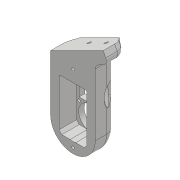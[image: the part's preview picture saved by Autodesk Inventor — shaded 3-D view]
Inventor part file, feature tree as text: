
AUTODESK INVENTOR PART (.ipt)
format: ipt  version: 2018 (Build 220112000, 112)  size: 900,608 bytes
history: native  units: mm
features: sketch x31, projected_geometry x26, extrude x24, hole x10, fillet x10, chamfer x3, mirror x1, plane x1
ambient origin geometry x8: Origin, YZ Plane, XZ Plane, XY Plane, X Axis, Y Axis, Z Axis, Center Point
bodies: Solid1 (feature_tree)
feature tree (106):
  extrude  "Extrusion1"  Depth=45.0mm
  extrude  "Extrusion2"  Depth=2.25mm
  hole  "Hole1"  [1 undecoded]
  hole  "Hole2"  [1 undecoded]
  fillet  "Fillet1"  Radius=14.0mm
  extrude  "Extrusion3"  Depth=18.5mm
  extrude  "Extrusion4"  Depth=10.0mm
  extrude  "Extrusion5"  Depth=2.195mm
  extrude  "Extrusion6"  Depth=20.5mm
  hole  "Hole3"  [1 undecoded]
  extrude  "Extrusion7"  Depth=0.5mm
  extrude  "Extrusion8"  Depth=5.0mm TaperAngle=0.0deg
  extrude  "Extrusion9"  Depth=10.0mm
  extrude  "Extrusion10"  Depth=10.0mm
  extrude  "Extrusion11"  Depth=14.5mm
  extrude  "Extrusion12"  Depth=20.0mm
  extrude  "Extrusion13"  Depth=5.0mm
  extrude  "Extrusion14"  Depth=5.0mm
  extrude  "Extrusion15"  Depth=5.0mm
  extrude  "Extrusion16"  Depth=5.0mm
  extrude  "Extrusion17"  Depth=4.0mm
  chamfer  "Chamfer1"  Distance=1.0mm
  fillet  "Fillet7"  Radius=20.7mm
  fillet  "Fillet8"  Radius=32.0mm
  mirror  "Mirror1"
  extrude  "Extrusion24"  Depth=5.0mm TaperAngle=0.0deg
  extrude  "Extrusion25"  Depth=8.0mm
  extrude  "Extrusion26"  Depth=0.2mm TaperAngle=0.0deg
  extrude  "Extrusion27"  Depth=0.5mm TaperAngle=0.0deg
  extrude  "Extrusion28"  Depth=5.0mm TaperAngle=0.0deg
  chamfer  "Chamfer5"  Distance=5.0mm
  fillet  "Fillet18"  Radius=0.2mm
  fillet  "Fillet19"  Radius=0.2mm
  extrude  "Extrusion29"  Depth=1.5mm
  chamfer  "Chamfer6"  Distance=70.0mm
  hole  "Hole10"  [1 undecoded]
  plane  "Work Plane2"
  hole  "Hole11"  [1 undecoded]
  fillet  "Fillet20"  Radius=10.0mm
  sketch  "Sketch43"  dims[d102=2.5mm d103=2.0mm d104=45.0deg d105=1.5mm]
  hole  "Hole12"  [1 undecoded]
  hole  "Hole13"  [1 undecoded]
  hole  "Hole14"  [1 undecoded]
  fillet  "Fillet21"  Radius=10.0mm
  fillet  "Fillet22"  Radius=2.0mm
  hole  "Hole15"  [1 undecoded]
  fillet  "Fillet23"  Radius=5.0mm
  hole  "Hole16"  [1 undecoded]
  fillet  "Fillet24"  Radius=15.0mm
  extrude  "Extrusion30"  Depth=10.0mm TaperAngle=0.0deg
  sketch  "Sketch1"  dims[d0=24.5mm d1=45.0mm]
  sketch  "Sketch2"  dims[d2=1.95mm d3=0.0mm d4=2.25mm]
  projected_geometry  "Projected Loop1"
  sketch  "Sketch3"  dims[d5=20.0mm d6=2.25mm]
  projected_geometry  "Projected Loop2"
  sketch  "Sketch4"  dims[d7=5.25mm d8=5.25mm d9=14.0mm]
  projected_geometry  "Projected Loop3"
  sketch  "Sketch5"  dims[d10=5.25mm d11=18.5mm]
  projected_geometry  "Projected Loop4"
  sketch  "Sketch6"  dims[d12=10.0mm d13=0.0mm d14=20.5mm]
  projected_geometry  "Projected Loop5"
  sketch  "Sketch7"  dims[d15=2.0mm d16=2.195mm]
  projected_geometry  "Projected Loop6"
  sketch  "Sketch8"  dims[d17=2.0mm]
  projected_geometry  "Projected Loop7"
  sketch  "Sketch9"  dims[d18=2.4mm d19=6.0mm d20=4.4mm d21=2.0mm d22=90.0deg d23=8.0mm d24=20.594885mm d25=20.5mm]
  projected_geometry  "Projected Loop8"
  projected_geometry  "Projected Loop9"
  sketch  "Sketch10"  dims[d26=26.65mm d27=2.0mm]
  projected_geometry  "Projected Loop10"
  projected_geometry  "Projected Loop11"
  sketch  "Sketch11"  dims[d28=2.0mm]
  projected_geometry  "Projected Loop12"
  sketch  "Sketch12"  dims[d29=2.4mm d30=6.0mm d31=4.4mm d32=2.0mm d33=90.0deg d34=8.0mm d35=20.594885mm d36=0.5mm]
  sketch  "Sketch13"  dims[d37=18.0mm d38=5.0mm d39=0.0mm]
  sketch  "Sketch14"  dims[d41=10.0mm d42=0.0mm d43=24.5mm]
  projected_geometry  "Projected Loop13"
  sketch  "Sketch15"  dims[d44=1.15mm d45=0.0mm d46=10.0mm]
  sketch  "Sketch16"  dims[d47=21.0mm d48=14.5mm]
  projected_geometry  "Projected Loop14"
  sketch  "Sketch17"  dims[d49=20.0mm d50=14.5mm]
  projected_geometry  "Projected Loop15"
  sketch  "Sketch18"  dims[d51=24.5mm d52=5.0mm]
  projected_geometry  "Projected Loop16"
  sketch  "Sketch19"  dims[d53=5.0mm d54=2.25mm]
  projected_geometry  "Projected Loop17"
  sketch  "Sketch20"  dims[d55=2.25mm d56=5.0mm]
  projected_geometry  "Projected Loop18"
  sketch  "Sketch35"  dims[d57=5.0mm d58=9.0mm]
  projected_geometry  "Projected Loop28"
  sketch  "Sketch36"  dims[d59=14.75mm d60=4.0mm d61=1.0mm d62=0.0mm d63=20.7mm]
  projected_geometry  "Projected Loop29"
  sketch  "Sketch37"  dims[d64=2.4mm d65=6.0mm d66=4.4mm d67=2.0mm d68=90.0deg d69=8.0mm d70=20.594885mm d72=32.0mm]
  sketch  "Sketch38"  dims[d73=5.0mm d74=0.0mm d75=1.0mm d76=0.0mm]
  sketch  "Sketch39"  dims[d77=12.25mm d78=0.0mm d80=8.0mm]
  projected_geometry  "Projected Loop30"
  sketch  "Sketch40"  dims[d81=4.5mm d82=0.0mm d84=0.2mm d85=0.0mm]
  projected_geometry  "Projected Loop31"
  sketch  "Sketch41"  dims[d86=21.0mm d87=0.5mm d88=0.0mm]
  projected_geometry  "Projected Loop32"
  projected_geometry  "Projected Loop33"
  sketch  "Sketch42"  dims[d91=8.0mm d92=0.0mm d93=5.0mm d94=0.0mm d95=5.0mm d96=0.0mm d98=0.2mm d99=0.0mm d100=0.2mm d101=0.0mm]
  projected_geometry  "Projected Loop34"
  sketch  "Sketch44"  dims[d114=0.5mm]
  projected_geometry  "Projected Loop35"
  sketch  "Sketch45"  dims[d187=40.0mm d188=70.0mm d189=20.0mm d190=10.0mm d191=0.0mm d192=10.0mm d193=0.0mm d194=2.0mm d195=0.0mm d196=2.0mm d197=0.0mm d198=8.0mm d199=10.0mm d200=2.0mm d201=0.0mm d204=7.0mm d205=2.0mm d206=45.0deg d207=5.0mm d208=8.0mm d209=15.0mm d210=2.0mm d211=0.0mm d212=1.5mm d213=2.0mm d214=45.0deg d215=24.0mm d216=17.0mm d217=3.5mm d218=3.2mm d219=6.0mm d220=9.4mm d221=2.0mm d222=90.0deg d223=8.0mm d224=20.594885mm d225=6.0mm d226=6.0mm d227=9.4mm d228=2.0mm d229=90.0deg d230=69.0mm d231=0.0mm d232=1.0mm d233=8.0mm d234=2.459mm d235=6.0mm d236=9.4mm d237=2.0mm d238=90.0deg d239=34.0mm d240=20.594885mm d241=3.2mm d242=6.0mm d243=6.3mm d244=2.0mm d245=90.0deg d246=20.55mm d247=0.0mm d248=6.0mm d249=6.0mm d250=6.3mm d251=2.0mm d252=90.0deg d253=10.0mm d254=0.0mm d255=1.5mm d256=0.75mm d257=4.0mm d258=6.0mm d259=4.4mm d260=2.0mm d261=90.0deg d262=2.5mm d263=0.0mm d264=1.0mm d265=4.0mm d266=6.0mm d267=4.4mm d268=2.0mm d269=90.0deg d270=2.5mm d271=0.0mm d272=1.0mm d273=20.55mm d274=0.0mm]
note: 10 required parameter values undecoded (feature->parameter linkage not recoverable at this tier; creation-order binding heuristic only, values carry confidence <= 0.55)
